# Revit family: LAMP_FIL 45 CORNER OPAL RECESSED
name_source: partatom
category: Luminarias
revit_build: Autodesk Revit 2018 (Build: 20170223_1515(x64)
units: mm (PartAtom-declared; Revit-internal decimal feet)

## family parameters
Anfitrión = Cara
Compartido = No
Corte con vacíos al cargar = No
Cota de conector redondo = Diámetro de uso
Origen de luz = Sí
Punto de cálculo de habitación = No
Tipo de pieza = Normal

## types (12) — shared parameters
CRI = 80
Cambio de temperatura de color de luz atenuada = <Ninguno>
Dimensions = 318x318
Elevación por defecto = 1219 mm
Fabricante = LAMP
Filtro de color = 16777215
Gear = Electronic
IEE = A+
Installation instructions = https://www.lamp.es
Insulation class = I
LED Lifetime = 70.000 L80 B10
Lamp = MID-POWER LED
Last update = 15/04/2021
MacAdam = 3
Manufacturer URL = http://www.lamp.es
Manufacturer country = Spain
Manufacturer name = LAMP
Material difusor = LAMP_PC Difusor Opal Fil
Material suspension = LAMP_Acero genérico
Power = 8 W
Power Supply = 220-240V 50/60Hz
Product URL = https://www.lamp.es
Product datasheet = http://www.lamp.es
Protection rating = IP20 / IK07
Recessed dimensions = 846x51x0
Type = MID POWER TRIDONIC
Weight = 1.32 kg
Ángulo de inclinación = -90.00°

## per-type parameters (varying)
| type | Archivo de red fotométrica | Descripción | Efficacy | Finish | Indirect light | Material perfil | Modelo | Plum | Product code |
| 1300LM 3000K  BLACK | F41RECRMOOP830NB.IES | FIL45 CORNER REC 1300 WW OPAL BK. | 86 lm/W | Matte black RAL 9011 | LAMP_FIL 45 CORNER OPAL RECESSED_INDIRECT : 1300LM 3000K | LAMP_Aluminio Perfil Fil NG | F41RECRMOOP830NB | 9 W | F41RECRMOOP830NB |
| 1300LM 3000K  GREY | F41RECRMOOP830NG.IES | FIL45 CORNER REC 1300 WW OPAL GR. | 86 lm/W | Gloss grey | LAMP_FIL 45 CORNER OPAL RECESSED_INDIRECT : 1300LM 3000K | LAMP_Aluminio Perfil Fil GR | F41RECRMOOP830NG | 9 W | F41RECRMOOP830NG |
| 1300LM 3000K  WHITE | F41RECRMOOP830NW.IES | FIL45 CORNER REC 1300 WW OPAL WH. | 86 lm/W | Matte white RAL 9010 | LAMP_FIL 45 CORNER OPAL RECESSED_INDIRECT : 1300LM 3000K | LAMP_Aluminio Perfil Fil BL | F41RECRMOOP830NW | 9 W | F41RECRMOOP830NW |
| 1300LM 4000K  BLACK | F41RECRMOOP840NB.IES | FIL45 CORNER REC 1300 NW OPAL BK. | 91 lm/W | Matte black RAL 9011 | LAMP_FIL 45 CORNER OPAL RECESSED_INDIRECT : 1300LM 4000K | LAMP_Aluminio Perfil Fil NG | F41RECRMOOP840NB | 9 W | F41RECRMOOP840NB |
| 1300LM 4000K  GREY | F41RECRMOOP840NG.IES | FIL45 CORNER REC 1300 NW OPAL GR. | 91 lm/W | Gloss grey | LAMP_FIL 45 CORNER OPAL RECESSED_INDIRECT : 1300LM 4000K | LAMP_Aluminio Perfil Fil GR | F41RECRMOOP840NG | 9 W | F41RECRMOOP840NG |
| 1300LM 4000K  WHITE | F41RECRMOOP840NW.IES | FIL45 CORNER REC 1300 NW OPAL WH. | 91 lm/W | Matte white RAL 9010 | LAMP_FIL 45 CORNER OPAL RECESSED_INDIRECT : 1300LM 4000K | LAMP_Aluminio Perfil Fil BL | F41RECRMOOP840NW | 9 W | F41RECRMOOP840NW |
| 1300LM 3000K DALI BLACK | F41RECRMOOP830nB.IES | FIL45 CORNER REC 1300 WW OPAL DALI BK. | 90 lm/W | Matte black RAL 9011 | LAMP_FIL 45 CORNER OPAL RECESSED_INDIRECT : 1300LM 3000K | LAMP_Aluminio Perfil Fil NG | F41RECRMOOP830DB | 10 W | F41RECRMOOP830DB |
| 1300LM 3000K DALI GREY | F41RECRMOOP830nG.IES | FIL45 CORNER REC 1300 WW OPAL DALI GR. | 90 lm/W | Gloss grey | LAMP_FIL 45 CORNER OPAL RECESSED_INDIRECT : 1300LM 3000K | LAMP_Aluminio Perfil Fil GR | F41RECRMOOP830DG | 10 W | F41RECRMOOP830DG |
| 1300LM 3000K DALI WHITE | F41RECRMOOP830nW.IES | FIL45 CORNER REC 1300 WW OPAL DALI WH. | 90 lm/W | Matte white RAL 9010 | LAMP_FIL 45 CORNER OPAL RECESSED_INDIRECT : 1300LM 3000K | LAMP_Aluminio Perfil Fil BL | F41RECRMOOP830DW | 10 W | F41RECRMOOP830DW |
| 1300LM 4000K DALI BLACK | F41RECRMOOP840nB.IES | FIL45 CORNER REC 1300 NW OPAL DALI BK. | 94 lm/W | Matte black RAL 9011 | LAMP_FIL 45 CORNER OPAL RECESSED_INDIRECT : 1300LM 4000K | LAMP_Aluminio Perfil Fil NG | F41RECRMOOP840DB | 10 W | F41RECRMOOP840DB |
| 1300LM 4000K DALI GREY | F41RECRMOOP840nG.IES | FIL45 CORNER REC 1300 NW OPAL DALI GR. | 94 lm/W | Gloss grey | LAMP_FIL 45 CORNER OPAL RECESSED_INDIRECT : 1300LM 4000K | LAMP_Aluminio Perfil Fil GR | F41RECRMOOP840DG | 10 W | F41RECRMOOP840DG |
| 1300LM 4000K DALI WHITE | F41RECRMOOP840nW.IES | FIL45 CORNER REC 1300 NW OPAL DALI WH. | 94 lm/W | Matte white RAL 9010 | LAMP_FIL 45 CORNER OPAL RECESSED_INDIRECT : 1300LM 4000K | LAMP_Aluminio Perfil Fil BL | F41RECRMOOP840DW | 10 W | F41RECRMOOP840DW |
